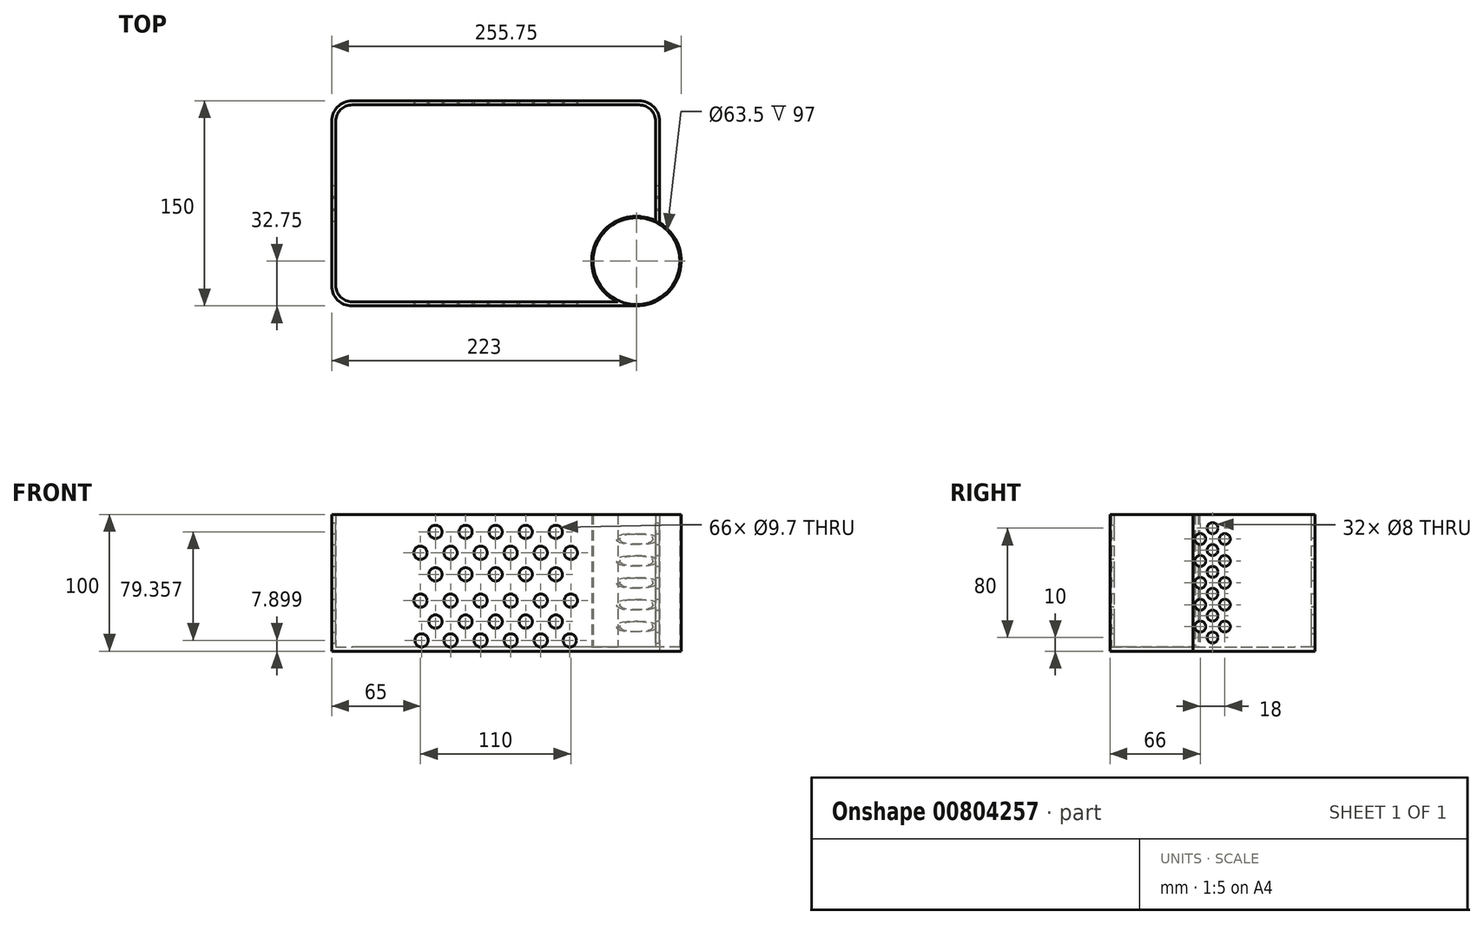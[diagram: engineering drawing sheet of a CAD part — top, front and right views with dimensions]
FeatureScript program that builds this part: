
annotation { "Feature Type Name" : "Feature", "Feature Type Description" : "" }
export const myFeature = defineFeature(function(context is Context, id is Id, definition is map)
    precondition{}
    {
        {
            var Q0;
            Q0=qCreatedBy(makeId("Top.planeOp"),FACE);
            var sketch = newSketch(context, id + "F0", { "sketchPlane" : qUnion([Q0])});
            skLineSegment(sketch, "E0.bottom", {"start": v(-105, 75) * mm, "end": v(105, 75) * mm});
            skLineSegment(sketch, "E0.top", {"start": v(-105, -75) * mm, "end": v(103, -75) * mm});
            skLineSegment(sketch, "E0.left", {"start": v(-120, 60) * mm, "end": v(-120, -60) * mm});
            skLineSegment(sketch, "E0.right", {"start": v(120, 60) * mm, "end": v(120, -14.26) * mm});
            skPoint(sketch, "E0.middle", {"position": v(0, 0) * mm});
            skPoint(sketch, "E1.visualSharp", {"position": v(-120, 75) * mm});
            skArc(sketch, "E1.filletArc", {"start": v(-105, 75) * mm, "mid": v(-115.6, 70.6) * mm, "end": v(-120, 60) * mm});
            skPoint(sketch, "E2.visualSharp", {"position": v(120, 75) * mm});
            skArc(sketch, "E2.filletArc", {"start": v(120, 60) * mm, "mid": v(115.6, 70.6) * mm, "end": v(105, 75) * mm});
            skPoint(sketch, "E3.visualSharp", {"position": v(120, -75) * mm});
            skPoint(sketch, "E4.visualSharp", {"position": v(-120, -75) * mm});
            skArc(sketch, "E4.filletArc", {"start": v(-120, -60) * mm, "mid": v(-115.6, -70.6) * mm, "end": v(-105, -75) * mm});
            skArc(sketch, "E5.0", {"start": v(-105, 72) * mm, "mid": v(-113.49, 68.49) * mm, "end": v(-117, 60) * mm});
            skLineSegment(sketch, "E5.1", {"start": v(-117, 60) * mm, "end": v(-117, -60) * mm});
            skLineSegment(sketch, "E5.2", {"start": v(-105, 72) * mm, "end": v(105, 72) * mm});
            skArc(sketch, "E5.3", {"start": v(-117, -60) * mm, "mid": v(-113.49, -68.49) * mm, "end": v(-105, -72) * mm});
            skArc(sketch, "E5.4", {"start": v(117, 60) * mm, "mid": v(113.49, 68.49) * mm, "end": v(105, 72) * mm});
            skLineSegment(sketch, "E5.5", {"start": v(117, 60) * mm, "end": v(117, -12.64) * mm});
            skLineSegment(sketch, "E5.7", {"start": v(-105, -72) * mm, "end": v(89.3, -72) * mm});
            skCircle(sketch, "E6", {"center": v(103, -42.25) * mm, "radius": 32.75 * mm});
            skCircle(sketch, "E7", {"center": v(103, -42.25) * mm, "radius": 31.75 * mm});
            skSolve(sketch);
        }
        {
            var Q0;
            Q0=makeQuery(id+"F0.imprint","IMPRINT",FACE,{"disambiguationData":[TD([[makeQuery(id+"F0.imprint","IMPRINT",EDGE,{"derivedFrom":sQuery(id+"F0.wireOp",EDGE,"E0.bottom")}),-1.0]])]});
            var Q1;
            Q1=makeQuery(id+"F0.imprint","IMPRINT",FACE,{"disambiguationData":[TD([[makeQuery(id+"F0.imprint","IMPRINT",EDGE,{"derivedFrom":sQuery(id+"F0.wireOp",EDGE,"E7")}),-1.0]])]});
            extrude(context, id + "F1", {"entities" : qUnion([Q0, Q1]), "flatOperationType" : FlatOperationType.REMOVE, "depth" : 100 * mm, "offsetDistance" : 25 * mm, "domain" : OperationDomain.MODEL});
        }
        {
            var Q0;
            Q0=qCreatedBy(makeId("Top.planeOp"),FACE);
            var sketch = newSketch(context, id + "F2", { "sketchPlane" : qUnion([Q0])});
            skLineSegment(sketch, "E8.bottom", {"start": v(107, -72) * mm, "end": v(-107, -72) * mm});
            skLineSegment(sketch, "E8.top", {"start": v(107, 72) * mm, "end": v(-107, 72) * mm});
            skLineSegment(sketch, "E8.left", {"start": v(117, -62) * mm, "end": v(117, 62) * mm});
            skLineSegment(sketch, "E8.right", {"start": v(-117, -62) * mm, "end": v(-117, 62) * mm});
            skPoint(sketch, "E8.middle", {"position": v(0, 0) * mm});
            skPoint(sketch, "E9.visualSharp", {"position": v(-117, -72) * mm});
            skArc(sketch, "E9.filletArc", {"start": v(-117, -62) * mm, "mid": v(-114.07, -69.07) * mm, "end": v(-107, -72) * mm});
            skPoint(sketch, "E10.visualSharp", {"position": v(-117, 72) * mm});
            skArc(sketch, "E10.filletArc", {"start": v(-107, 72) * mm, "mid": v(-114.07, 69.07) * mm, "end": v(-117, 62) * mm});
            skPoint(sketch, "E11.visualSharp", {"position": v(117, 72) * mm});
            skArc(sketch, "E11.filletArc", {"start": v(117, 62) * mm, "mid": v(114.07, 69.07) * mm, "end": v(107, 72) * mm});
            skPoint(sketch, "E12.visualSharp", {"position": v(117, -72) * mm});
            skArc(sketch, "E12.filletArc", {"start": v(107, -72) * mm, "mid": v(114.07, -69.07) * mm, "end": v(117, -62) * mm});
            skCircle(sketch, "E13", {"center": v(103, -42.25) * mm, "radius": 32.75 * mm});
            skSolve(sketch);
        }
        {
            var Q0;
            Q0 = qSketchRegion(id + "F2", true);
            extrude(context, id + "F3", {"entities" : qUnion([Q0]), "operationType" : NewBodyOperationType.ADD, "depth" : 3 * mm, "offsetDistance" : 25 * mm});
        }
        {
            var Q0;
            Q0=makeQuery(id+"F1.opExtrude","SWEPT_FACE",FACE,{"disambiguationData":[OSD([sQuery(id+"F0.wireOp",EDGE,"E0.top")])]});
            var sketch = newSketch(context, id + "F4", { "sketchPlane" : qUnion([Q0])});
            skPoint(sketch, "E14", {"position": v(-55, 71.93) * mm});
            skPoint(sketch, "E15", {"position": v(-55, 36.97) * mm});
            skPoint(sketch, "E16", {"position": v(-54.21, 7.9) * mm});
            skPoint(sketch, "E17", {"position": v(-33, 7.9) * mm});
            skPoint(sketch, "E18", {"position": v(-44, 21.65) * mm});
            skPoint(sketch, "E19", {"position": v(-33, 36.97) * mm});
            skPoint(sketch, "E20", {"position": v(-44, 56.22) * mm});
            skPoint(sketch, "E21", {"position": v(-33, 71.93) * mm});
            skPoint(sketch, "E22", {"position": v(-44, 87.26) * mm});
            skPoint(sketch, "E23", {"position": v(-11, 7.9) * mm});
            skPoint(sketch, "E24", {"position": v(-22, 21.65) * mm});
            skPoint(sketch, "E25", {"position": v(-11, 36.97) * mm});
            skPoint(sketch, "E26", {"position": v(-22, 56.22) * mm});
            skPoint(sketch, "E27", {"position": v(-11, 71.93) * mm});
            skPoint(sketch, "E28", {"position": v(-22, 87.26) * mm});
            skPoint(sketch, "E29", {"position": v(0, 56.22) * mm});
            skPoint(sketch, "E30", {"position": v(0, 21.65) * mm});
            skPoint(sketch, "E31", {"position": v(0, 87.26) * mm});
            skPoint(sketch, "E32.MirrorP", {"position": v(55, 71.93) * mm});
            skPoint(sketch, "E33.MirrorP", {"position": v(44, 87.26) * mm});
            skPoint(sketch, "E34.MirrorP", {"position": v(33, 71.93) * mm});
            skPoint(sketch, "E35.MirrorP", {"position": v(22, 87.26) * mm});
            skPoint(sketch, "E36.MirrorP", {"position": v(11, 71.93) * mm});
            skPoint(sketch, "E37.MirrorP", {"position": v(11, 36.97) * mm});
            skPoint(sketch, "E38.MirrorP", {"position": v(22, 56.22) * mm});
            skPoint(sketch, "E39.MirrorP", {"position": v(33, 36.97) * mm});
            skPoint(sketch, "E40.MirrorP", {"position": v(44, 56.22) * mm});
            skPoint(sketch, "E41.MirrorP", {"position": v(55, 36.97) * mm});
            skPoint(sketch, "E42.MirrorP", {"position": v(54.21, 7.9) * mm});
            skPoint(sketch, "E43.MirrorP", {"position": v(44, 21.65) * mm});
            skPoint(sketch, "E44.MirrorP", {"position": v(33, 7.9) * mm});
            skPoint(sketch, "E45.MirrorP", {"position": v(22, 21.65) * mm});
            skPoint(sketch, "E46.MirrorP", {"position": v(11, 7.9) * mm});
            skSolve(sketch);
        }
        {
            var Q0;
            Q0=sQuery(id+"F4.wireOp",VERTEX,"1249680f-0854-464a-9f1d-6e637db3273b");
            var Q1;
            Q1=sQuery(id+"F4.wireOp",VERTEX,"c48a611a-5515-48cc-8b3c-c64361452e84");
            var Q2;
            Q2=sQuery(id+"F4.wireOp",VERTEX,"feedc4c1-4209-4d13-8166-2d8d50b1ba46");
            var Q3;
            Q3=sQuery(id+"F4.wireOp",VERTEX,"E22");
            var Q4;
            Q4=sQuery(id+"F4.wireOp",VERTEX,"E14");
            var Q5;
            Q5=sQuery(id+"F4.wireOp",VERTEX,"E21");
            var Q6;
            Q6=sQuery(id+"F4.wireOp",VERTEX,"E28");
            var Q7;
            Q7=sQuery(id+"F4.wireOp",VERTEX,"E27");
            var Q8;
            Q8=sQuery(id+"F4.wireOp",VERTEX,"E31");
            var Q9;
            Q9=sQuery(id+"F4.wireOp",VERTEX,"E36.MirrorP");
            var Q10;
            Q10=sQuery(id+"F4.wireOp",VERTEX,"E35.MirrorP");
            var Q11;
            Q11=sQuery(id+"F4.wireOp",VERTEX,"E34.MirrorP");
            var Q12;
            Q12=sQuery(id+"F4.wireOp",VERTEX,"E33.MirrorP");
            var Q13;
            Q13=sQuery(id+"F4.wireOp",VERTEX,"E32.MirrorP");
            var Q14;
            Q14=sQuery(id+"F4.wireOp",VERTEX,"2f3a7c9b-3485-48b0-8421-3c0acd69274b0.MirrorP");
            var Q15;
            Q15=sQuery(id+"F4.wireOp",VERTEX,"58801b24-945d-4a84-9361-3bb489527c0f0.MirrorP");
            var Q16;
            Q16=sQuery(id+"F4.wireOp",VERTEX,"121eff00-b3f2-4d73-9581-48acd3f356fc0.MirrorP");
            var Q17;
            Q17=sQuery(id+"F4.wireOp",VERTEX,"53a6c2e9-6bb1-4512-9243-d6ab151918240.MirrorP");
            var Q18;
            Q18=sQuery(id+"F4.wireOp",VERTEX,"cd84fa74-b1df-46dd-9266-e3eb57c021540.MirrorP");
            var Q19;
            Q19=sQuery(id+"F4.wireOp",VERTEX,"b589993c-7808-4f65-b466-26c857e696a70.MirrorP");
            var Q20;
            Q20=sQuery(id+"F4.wireOp",VERTEX,"E41.MirrorP");
            var Q21;
            Q21=sQuery(id+"F4.wireOp",VERTEX,"E40.MirrorP");
            var Q22;
            Q22=sQuery(id+"F4.wireOp",VERTEX,"E39.MirrorP");
            var Q23;
            Q23=sQuery(id+"F4.wireOp",VERTEX,"E38.MirrorP");
            var Q24;
            Q24=sQuery(id+"F4.wireOp",VERTEX,"E37.MirrorP");
            var Q25;
            Q25=sQuery(id+"F4.wireOp",VERTEX,"E29");
            var Q26;
            Q26=sQuery(id+"F4.wireOp",VERTEX,"E25");
            var Q27;
            Q27=sQuery(id+"F4.wireOp",VERTEX,"E19");
            var Q28;
            Q28=sQuery(id+"F4.wireOp",VERTEX,"E26");
            var Q29;
            Q29=sQuery(id+"F4.wireOp",VERTEX,"E20");
            var Q30;
            Q30=sQuery(id+"F4.wireOp",VERTEX,"7efd427e-9d30-4ea2-a530-80f85d0640cf");
            var Q31;
            Q31=sQuery(id+"F4.wireOp",VERTEX,"E15");
            var Q32;
            Q32=sQuery(id+"F4.wireOp",VERTEX,"c89d540b-1b15-49ee-8f93-578eb30a6c1b");
            var Q33;
            Q33=sQuery(id+"F4.wireOp",VERTEX,"1ddff87b-f5ff-442a-89eb-54ab217713a5");
            var Q34;
            Q34=sQuery(id+"F4.wireOp",VERTEX,"fa53c1d8-f26e-45ce-89ce-d3810ce8de11");
            var Q35;
            Q35=sQuery(id+"F4.wireOp",VERTEX,"3a890c22-6d18-4722-b26e-5d5742593684");
            var Q36;
            Q36=sQuery(id+"F4.wireOp",VERTEX,"ac3b581b-6db6-494a-91c2-55726dc97efb");
            var Q37;
            Q37=sQuery(id+"F4.wireOp",VERTEX,"E16");
            var Q38;
            Q38=sQuery(id+"F4.wireOp",VERTEX,"E18");
            var Q39;
            Q39=sQuery(id+"F4.wireOp",VERTEX,"E17");
            var Q40;
            Q40=sQuery(id+"F4.wireOp",VERTEX,"E24");
            var Q41;
            Q41=sQuery(id+"F4.wireOp",VERTEX,"E23");
            var Q42;
            Q42=sQuery(id+"F4.wireOp",VERTEX,"E30");
            var Q43;
            Q43=sQuery(id+"F4.wireOp",VERTEX,"E46.MirrorP");
            var Q44;
            Q44=sQuery(id+"F4.wireOp",VERTEX,"E45.MirrorP");
            var Q45;
            Q45=sQuery(id+"F4.wireOp",VERTEX,"E44.MirrorP");
            var Q46;
            Q46=sQuery(id+"F4.wireOp",VERTEX,"E43.MirrorP");
            var Q47;
            Q47=sQuery(id+"F4.wireOp",VERTEX,"E42.MirrorP");
            var Q48;
            Q48=sQuery(id+"F4.wireOp",VERTEX,"644691d1-73b9-436e-b62e-82853f2e291e0.MirrorP");
            var Q49;
            Q49=sQuery(id+"F4.wireOp",VERTEX,"83cbc3a2-61fc-4416-b40c-e07a24e0be620.MirrorP");
            var Q50;
            Q50=sQuery(id+"F4.wireOp",VERTEX,"ab588192-231d-42a0-bd55-d74e4c9267420.MirrorP");
            var Q51;
            Q51=makeQuery(id+"F1.opExtrude","SWEPT_BODY",BODY,{"disambiguationData":[OSD([sQuery(id+"F0.wireOp",EDGE,"E0.bottom"),sQuery(id+"F0.wireOp",EDGE,"E0.top"),sQuery(id+"F0.wireOp",EDGE,"E0.left"),sQuery(id+"F0.wireOp",EDGE,"E0.right"),sQuery(id+"F0.wireOp",EDGE,"E1.filletArc"),sQuery(id+"F0.wireOp",EDGE,"E2.filletArc"),sQuery(id+"F0.wireOp",EDGE,"E3.filletArc"),sQuery(id+"F0.wireOp",EDGE,"E4.filletArc"),sQuery(id+"F0.wireOp",EDGE,"E5.0"),sQuery(id+"F0.wireOp",EDGE,"E5.1"),sQuery(id+"F0.wireOp",EDGE,"E5.2"),sQuery(id+"F0.wireOp",EDGE,"E5.3"),sQuery(id+"F0.wireOp",EDGE,"E5.4"),sQuery(id+"F0.wireOp",EDGE,"E5.5"),sQuery(id+"F0.wireOp",EDGE,"E5.6"),sQuery(id+"F0.wireOp",EDGE,"E5.7")])]});
            hole(context, id + "F5", {"style" : HoleStyle.SIMPLE, "endStyle" : HoleEndStyle.THROUGH, "holeDiameter" : 9.7 * mm, "majorDiameter" : 5 * mm, "isTappedThrough" : true, "tappedDepth" : 12 * mm, "tapClearance" : 3, "locations" : qUnion([Q0, Q1, Q2, Q3, Q4, Q5, Q6, Q7, Q8, Q9, Q10, Q11, Q12, Q13, Q14, Q15, Q16, Q17, Q18, Q19, Q20, Q21, Q22, Q23, Q24, Q25, Q26, Q27, Q28, Q29, Q30, Q31, Q32, Q33, Q34, Q35, Q36, Q37, Q38, Q39, Q40, Q41, Q42, Q43, Q44, Q45, Q46, Q47, Q48, Q49, Q50]), "scope" : qUnion([Q51])});
        }
        {
            var Q0;
            Q0=makeQuery(id+"F1.opExtrude","SWEPT_FACE",FACE,{"disambiguationData":[OSD([sQuery(id+"F0.wireOp",EDGE,"E0.right")])]});
            var sketch = newSketch(context, id + "F6", { "sketchPlane" : qUnion([Q0])});
            skPoint(sketch, "E47", {"position": v(0, 10) * mm});
            skPoint(sketch, "E48", {"position": v(0, 26) * mm});
            skPoint(sketch, "E49", {"position": v(0, 42) * mm});
            skPoint(sketch, "E50", {"position": v(0, 58) * mm});
            skPoint(sketch, "E51", {"position": v(0, 74) * mm});
            skPoint(sketch, "E52", {"position": v(0, 90) * mm});
            skPoint(sketch, "E53", {"position": v(9, 50) * mm});
            skPoint(sketch, "E54", {"position": v(-9, 50) * mm});
            skPoint(sketch, "E55", {"position": v(-9, 34) * mm});
            skPoint(sketch, "E56", {"position": v(-9, 18) * mm});
            skPoint(sketch, "E57", {"position": v(-9, 66) * mm});
            skPoint(sketch, "E58", {"position": v(-9, 82) * mm});
            skPoint(sketch, "E59", {"position": v(9, 82) * mm});
            skPoint(sketch, "E60", {"position": v(9, 66) * mm});
            skPoint(sketch, "E61", {"position": v(9, 34) * mm});
            skPoint(sketch, "E62", {"position": v(9, 18) * mm});
            skSolve(sketch);
        }
        {
            var Q0;
            Q0=sQuery(id+"F6.wireOp",VERTEX,"E52");
            var Q1;
            Q1=sQuery(id+"F6.wireOp",VERTEX,"E51");
            var Q2;
            Q2=sQuery(id+"F6.wireOp",VERTEX,"E50");
            var Q3;
            Q3=sQuery(id+"F6.wireOp",VERTEX,"E53");
            var Q4;
            Q4=sQuery(id+"F6.wireOp",VERTEX,"E54");
            var Q5;
            Q5=sQuery(id+"F6.wireOp",VERTEX,"E49");
            var Q6;
            Q6=sQuery(id+"F6.wireOp",VERTEX,"E48");
            var Q7;
            Q7=sQuery(id+"F6.wireOp",VERTEX,"E47");
            var Q8;
            Q8=sQuery(id+"F6.wireOp",VERTEX,"E58");
            var Q9;
            Q9=sQuery(id+"F6.wireOp",VERTEX,"E57");
            var Q10;
            Q10=sQuery(id+"F6.wireOp",VERTEX,"E55");
            var Q11;
            Q11=sQuery(id+"F6.wireOp",VERTEX,"E56");
            var Q12;
            Q12=sQuery(id+"F6.wireOp",VERTEX,"E59");
            var Q13;
            Q13=sQuery(id+"F6.wireOp",VERTEX,"E60");
            var Q14;
            Q14=sQuery(id+"F6.wireOp",VERTEX,"E61");
            var Q15;
            Q15=sQuery(id+"F6.wireOp",VERTEX,"E62");
            var Q16;
            Q16=makeQuery(id+"F1.opExtrude","SWEPT_BODY",BODY,{"disambiguationData":[OSD([sQuery(id+"F0.wireOp",EDGE,"E0.bottom"),sQuery(id+"F0.wireOp",EDGE,"E0.top"),sQuery(id+"F0.wireOp",EDGE,"E0.left"),sQuery(id+"F0.wireOp",EDGE,"E0.right"),sQuery(id+"F0.wireOp",EDGE,"E1.filletArc"),sQuery(id+"F0.wireOp",EDGE,"E2.filletArc"),sQuery(id+"F0.wireOp",EDGE,"E4.filletArc"),sQuery(id+"F0.wireOp",EDGE,"E5.0"),sQuery(id+"F0.wireOp",EDGE,"E5.1"),sQuery(id+"F0.wireOp",EDGE,"E5.2"),sQuery(id+"F0.wireOp",EDGE,"E5.3"),sQuery(id+"F0.wireOp",EDGE,"E5.4"),sQuery(id+"F0.wireOp",EDGE,"E5.5"),sQuery(id+"F0.wireOp",EDGE,"E5.7"),sQuery(id+"F0.wireOp",EDGE,"E6"),sQuery(id+"F0.wireOp",EDGE,"E7")])]});
            hole(context, id + "F7", {"style" : HoleStyle.SIMPLE, "endStyle" : HoleEndStyle.THROUGH, "holeDiameter" : 8 * mm, "majorDiameter" : 5 * mm, "isTappedThrough" : true, "tappedDepth" : 12 * mm, "tapClearance" : 3, "locations" : qUnion([Q0, Q1, Q2, Q3, Q4, Q5, Q6, Q7, Q8, Q9, Q10, Q11, Q12, Q13, Q14, Q15]), "scope" : qUnion([Q16])});
        }
    });
